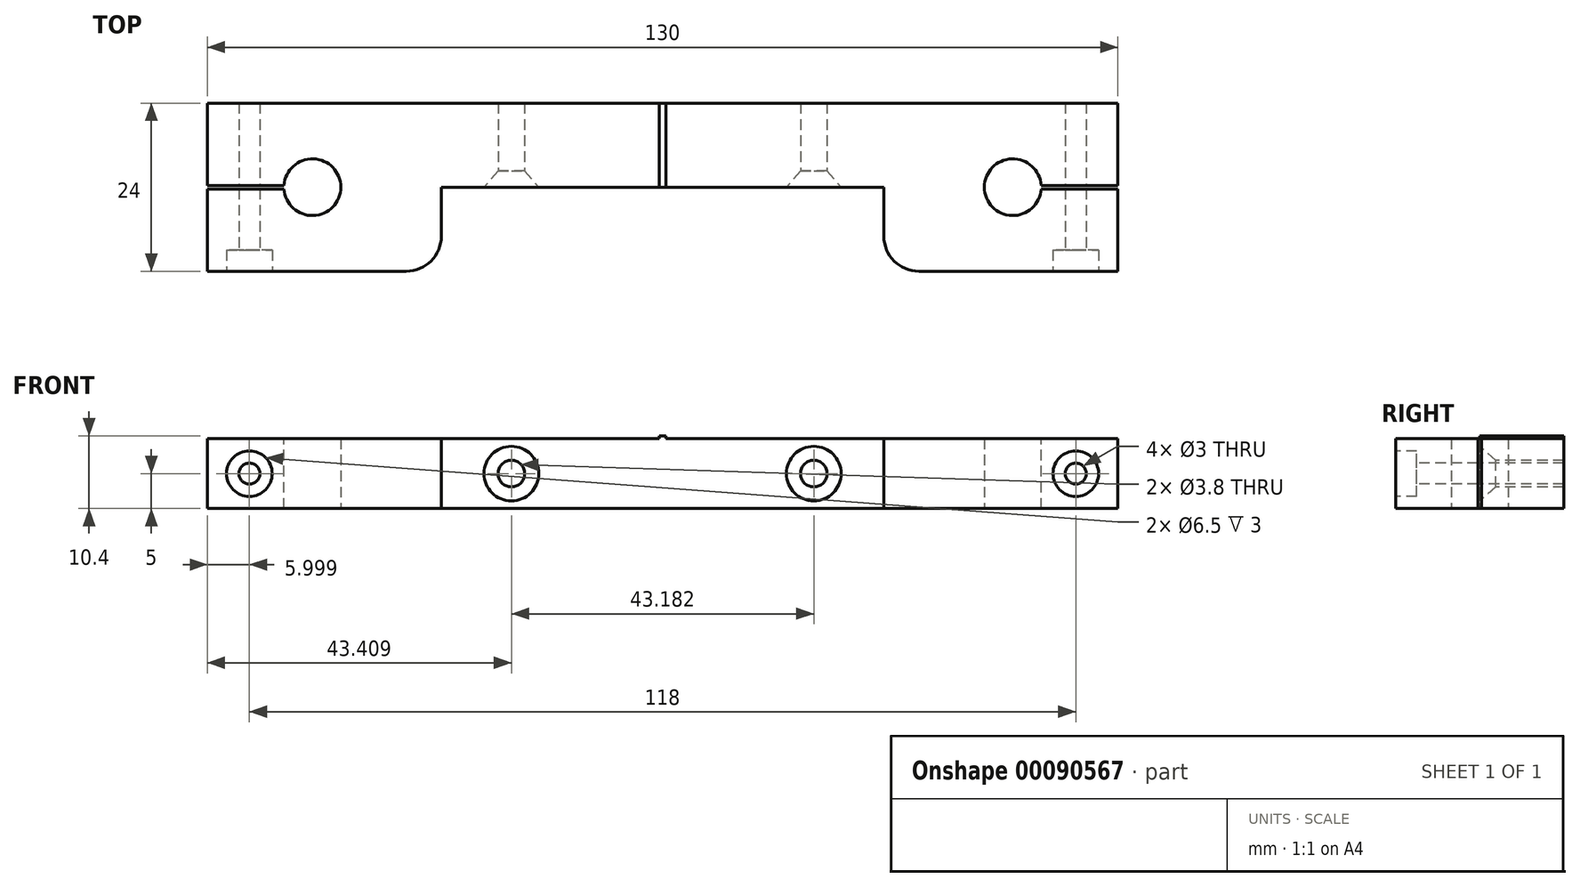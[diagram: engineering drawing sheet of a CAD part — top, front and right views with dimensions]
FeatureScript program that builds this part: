
annotation { "Feature Type Name" : "Feature", "Feature Type Description" : "" }
export const myFeature = defineFeature(function(context is Context, id is Id, definition is map)
    precondition{}
    {
        {
            var Q0;
            Q0=qCreatedBy(makeId("Top.planeOp"),FACE);
            var sketch = newSketch(context, id + "F0", { "sketchPlane" : qUnion([Q0])});
            skLineSegment(sketch, "E0.bottom", {"start": v(-62.4, -8.21) * mm, "end": v(67.6, -8.21) * mm});
            skLineSegment(sketch, "E0.top", {"start": v(-62.4, -32.21) * mm, "end": v(67.6, -32.21) * mm});
            skLineSegment(sketch, "E0.left", {"start": v(-62.4, -8.21) * mm, "end": v(-62.4, -32.21) * mm});
            skLineSegment(sketch, "E0.right", {"start": v(67.6, -8.21) * mm, "end": v(67.6, -32.21) * mm});
            skLineSegment(sketch, "E1", {"start": v(-62.4, -20.21) * mm, "end": v(67.6, -20.21) * mm, "construction": true});
            skLineSegment(sketch, "E2", {"start": v(-47.4, -8.21) * mm, "end": v(-47.4, -32.21) * mm, "construction": true});
            skCircle(sketch, "E3", {"center": v(-47.4, -20.21) * mm, "radius": 4.05 * mm});
            skCircle(sketch, "E4.1.0.0", {"center": v(52.6, -20.21) * mm, "radius": 4.05 * mm});
            skLineSegment(sketch, "E4.direction1", {"start": v(-47.4, -20.21) * mm, "end": v(52.6, -20.21) * mm, "construction": true});
            skPoint(sketch, "E5", {"position": v(2.6, -32.21) * mm});
            skLineSegment(sketch, "E6.bottom", {"start": v(-29, -32.21) * mm, "end": v(34.2, -32.21) * mm});
            skLineSegment(sketch, "E6.top", {"start": v(-29, -20.21) * mm, "end": v(34.2, -20.21) * mm});
            skLineSegment(sketch, "E6.left", {"start": v(-29, -32.21) * mm, "end": v(-29, -20.21) * mm});
            skLineSegment(sketch, "E6.right", {"start": v(34.2, -32.21) * mm, "end": v(34.2, -20.21) * mm});
            skPoint(sketch, "E7", {"position": v(2.6, -20.21) * mm});
            skSolve(sketch);
        }
        {
            var Q0;
            Q0=makeQuery(id+"F0.imprint","IMPRINT",FACE,{"disambiguationData":[TD([[makeQuery(id+"F0.imprint","IMPRINT",EDGE,{"derivedFrom":sQuery(id+"F0.wireOp",EDGE,"E0.bottom")}),-1.0]])]});
            extrude(context, id + "F1", {"entities" : qUnion([Q0]), "depth" : 10 * mm});
        }
        {
            var Q0;
            Q0=makeQuery(id+"F1.opExtrude","SWEPT_EDGE",EDGE,{"disambiguationData":[OSD([sQuery(id+"F0.wireOp",EDGE,"E0.top"),sQuery(id+"F0.wireOp",EDGE,"E6.bottom"),sQuery(id+"F0.wireOp",EDGE,"E6.right")])]});
            var Q1;
            Q1=makeQuery(id+"F1.opExtrude","SWEPT_EDGE",EDGE,{"disambiguationData":[OSD([sQuery(id+"F0.wireOp",EDGE,"E0.top"),sQuery(id+"F0.wireOp",EDGE,"E6.bottom"),sQuery(id+"F0.wireOp",EDGE,"E6.left")])]});
            fillet(context, id + "F2", {"entities" : qUnion([Q0, Q1]), "radius" : 5 * mm, "tangentPropagation" : true, "allowEdgeOverflow" : false});
        }
        {
            var Q0;
            Q0=makeQuery(id+"F1.opExtrude","SWEPT_FACE",FACE,{"disambiguationData":[OSD([sQuery(id+"F0.wireOp",EDGE,"E6.top")])]});
            var sketch = newSketch(context, id + "F3", { "sketchPlane" : qUnion([Q0])});
            skLineSegment(sketch, "E8", {"start": v(-29, 5) * mm, "end": v(34.2, 5) * mm, "construction": true});
            skLineSegment(sketch, "E9", {"start": v(-19, 10) * mm, "end": v(-19, 0) * mm, "construction": true});
            skLineSegment(sketch, "E10", {"start": v(24.2, 10) * mm, "end": v(24.2, 0) * mm, "construction": true});
            skPoint(sketch, "E11", {"position": v(-19, 5) * mm});
            skPoint(sketch, "E12", {"position": v(24.2, 5) * mm});
            skSolve(sketch);
        }
        {
            var Q0;
            Q0=sQuery(id+"F3.wireOp",VERTEX,"E11");
            var Q1;
            Q1=sQuery(id+"F3.wireOp",VERTEX,"E12");
            var Q2;
            Q2=makeQuery(id+"F1.opExtrude","SWEPT_BODY",BODY,{"disambiguationData":[OSD([sQuery(id+"F0.wireOp",EDGE,"E0.bottom"),sQuery(id+"F0.wireOp",EDGE,"E0.top"),sQuery(id+"F0.wireOp",EDGE,"E0.left"),sQuery(id+"F0.wireOp",EDGE,"E0.right"),sQuery(id+"F0.wireOp",EDGE,"E3"),sQuery(id+"F0.wireOp",EDGE,"E4.1.0.0"),sQuery(id+"F0.wireOp",EDGE,"E6.top"),sQuery(id+"F0.wireOp",EDGE,"E6.left"),sQuery(id+"F0.wireOp",EDGE,"E6.right")])]});
            hole(context, id + "F4", {"style" : HoleStyle.C_SINK, "endStyle" : HoleEndStyle.THROUGH, "standardTappedOrClearance" : lookupTablePath({ "standard" : "ANSI", "fit" : "Normal (ASME)", "size" : "#6", "type" : "Clearance" }), "standardBlindInLast" : lookupTablePath({ "fit" : "Free", "standard" : "ANSI", "size" : "#6", "type" : "Clearance" }), "holeDiameter" : 3.8 * mm, "cSinkDiameter" : 7.8 * mm, "cSinkAngle" : 82 * degree, "locations" : qUnion([Q0, Q1]), "scope" : qUnion([Q2]), "isTappedThrough" : true});
        }
        {
            var Q0;
            Q0=makeQuery(id+"F1.opExtrude","CAP_FACE",FACE,{"disambiguationData":[OSD([sQuery(id+"F0.wireOp",EDGE,"E0.bottom"),sQuery(id+"F0.wireOp",EDGE,"E0.top"),sQuery(id+"F0.wireOp",EDGE,"E0.left"),sQuery(id+"F0.wireOp",EDGE,"E0.right"),sQuery(id+"F0.wireOp",EDGE,"E3"),sQuery(id+"F0.wireOp",EDGE,"E4.1.0.0"),sQuery(id+"F0.wireOp",EDGE,"E6.top"),sQuery(id+"F0.wireOp",EDGE,"E6.left"),sQuery(id+"F0.wireOp",EDGE,"E6.right")])],"isStart":false});
            var sketch = newSketch(context, id + "F5", { "sketchPlane" : qUnion([Q0])});
            skPoint(sketch, "E13", {"position": v(2.6, -8.21) * mm});
            skPoint(sketch, "E14", {"position": v(2.6, -20.21) * mm});
            skLineSegment(sketch, "E15", {"start": v(2.1, -8.21) * mm, "end": v(2.1, -20.21) * mm});
            skLineSegment(sketch, "E16", {"start": v(3.1, -8.21) * mm, "end": v(3.1, -20.21) * mm});
            skSolve(sketch);
        }
        {
            var Q0;
            {var subQ0=sQuery(id+"F5.wireOp",EDGE,"E15");Q0=makeQuery(id+"F5.imprint","IMPRINT",FACE,{"disambiguationData":[TD([[makeQuery(id+"F5.imprint","IMPRINT",EDGE,{"derivedFrom":subQ0}),1.0]])]});}
            extrude(context, id + "F6", {"entities" : qUnion([Q0]), "operationType" : NewBodyOperationType.ADD, "depth" : 0.4 * mm});
        }
        {
            var Q0;
            {var subQ0=sQuery(id+"F0.wireOp",EDGE,"E3");var subQ1=sQuery(id+"F0.wireOp",EDGE,"E0.left");var subQ2=sQuery(id+"F0.wireOp",EDGE,"E0.top");var subQ3=sQuery(id+"F0.wireOp",EDGE,"E6.left");var subQ5=sQuery(id+"F0.wireOp",EDGE,"E0.bottom");var subQ6=sQuery(id+"F0.wireOp",EDGE,"E6.top");Q0=makeQuery(id+"F6.boolean.opBoolean","SPLIT",FACE,{"disambiguationData":[TD([makeQuery(id+"F1.opExtrude","SWEPT_FACE",FACE,{"disambiguationData":[OSD([subQ1])]})])],"derivedFrom":makeQuery(id+"F1.opExtrude","CAP_FACE",FACE,{"disambiguationData":[OSD([subQ5,subQ2,subQ1,sQuery(id+"F0.wireOp",EDGE,"E0.right"),subQ0,sQuery(id+"F0.wireOp",EDGE,"E4.1.0.0"),subQ6,subQ3,sQuery(id+"F0.wireOp",EDGE,"E6.right")])],"isStart":false})});}
            var sketch = newSketch(context, id + "F7", { "sketchPlane" : qUnion([Q0])});
            skLineSegment(sketch, "E17.bottom", {"start": v(-62.4, -19.96) * mm, "end": v(-51.44, -19.96) * mm});
            skLineSegment(sketch, "E17.top", {"start": v(-62.4, -20.46) * mm, "end": v(-51.44, -20.46) * mm});
            skLineSegment(sketch, "E17.left", {"start": v(-62.4, -19.96) * mm, "end": v(-62.4, -20.46) * mm});
            skLineSegment(sketch, "E17.right", {"start": v(-51.44, -19.96) * mm, "end": v(-51.44, -20.46) * mm});
            skCircle(sketch, "E18.0", {"center": v(-47.4, -20.21) * mm, "radius": 4.05 * mm});
            skPoint(sketch, "E19", {"position": v(-51.44, -20.21) * mm});
            skCircle(sketch, "E20.0", {"center": v(52.6, -20.21) * mm, "radius": 4.05 * mm});
            skLineSegment(sketch, "E21.bottom", {"start": v(56.64, -19.96) * mm, "end": v(67.6, -19.96) * mm});
            skLineSegment(sketch, "E21.top", {"start": v(56.64, -20.46) * mm, "end": v(67.6, -20.46) * mm});
            skLineSegment(sketch, "E21.left", {"start": v(56.64, -19.96) * mm, "end": v(56.64, -20.46) * mm});
            skLineSegment(sketch, "E21.right", {"start": v(67.6, -19.96) * mm, "end": v(67.6, -20.46) * mm});
            skPoint(sketch, "E22", {"position": v(56.64, -20.21) * mm});
            skSolve(sketch);
        }
        {
            var Q0;
            {var subQ1=sQuery(id+"F7.wireOp",EDGE,"E21.bottom");Q0=makeQuery(id+"F7.imprint","IMPRINT",FACE,{"disambiguationData":[TD([[makeQuery(id+"F7.imprint","IMPRINT",EDGE,{"derivedFrom":subQ1}),-1.0]])]});}
            var Q1;
            {var subQ0=sQuery(id+"F7.wireOp",EDGE,"E17.bottom");Q1=makeQuery(id+"F7.imprint","IMPRINT",FACE,{"disambiguationData":[TD([[makeQuery(id+"F7.imprint","IMPRINT",EDGE,{"derivedFrom":subQ0}),-1.0]])]});}
            var Q2;
            {var subQ0=sQuery(id+"F7.wireOp",EDGE,"E17.right");Q2=makeQuery(id+"F7.imprint","IMPRINT",FACE,{"disambiguationData":[TD([[makeQuery(id+"F7.imprint","IMPRINT",EDGE,{"derivedFrom":subQ0}),-1.0]])]});}
            var Q3;
            {var subQ0=sQuery(id+"F7.wireOp",EDGE,"E21.left");Q3=makeQuery(id+"F7.imprint","IMPRINT",FACE,{"disambiguationData":[TD([[makeQuery(id+"F7.imprint","IMPRINT",EDGE,{"derivedFrom":subQ0}),1.0]])]});}
            extrude(context, id + "F8", {"entities" : qUnion([Q0, Q1, Q2, Q3]), "operationType" : NewBodyOperationType.REMOVE, "oppositeDirection" : true, "depth" : 25 * mm});
        }
        {
            var Q0;
            {var subQ0=sQuery(id+"F0.wireOp",EDGE,"E0.top");Q0=makeQuery(id+"F1.opExtrude","SWEPT_FACE",FACE,{"disambiguationData":[OSD([subQ0]),TDD([makeQuery(id+"F0.imprint","IMPRINT",EDGE,{"disambiguationData":[TD([[makeQuery(id+"F0.imprint","INTERSECT",VERTEX,{"derivedFrom":[subQ0,sQuery(id+"F0.wireOp",EDGE,"E0.left")]}),-1.0]])],"derivedFrom":subQ0})])]});}
            var sketch = newSketch(context, id + "F9", { "sketchPlane" : qUnion([Q0])});
            skLineSegment(sketch, "E23", {"start": v(-62.4, 5) * mm, "end": v(-34, 5) * mm, "construction": true});
            skLineSegment(sketch, "E24", {"start": v(-56.4, 10) * mm, "end": v(-56.4, 0) * mm, "construction": true});
            skPoint(sketch, "E25", {"position": v(-56.4, 5) * mm});
            skLineSegment(sketch, "E26.0.0", {"start": v(67.6, 10) * mm, "end": v(39.2, 10) * mm});
            skLineSegment(sketch, "E26.0.1", {"start": v(39.2, 10) * mm, "end": v(39.2, 0) * mm});
            skLineSegment(sketch, "E26.0.2", {"start": v(39.2, 0) * mm, "end": v(67.6, 0) * mm});
            skLineSegment(sketch, "E26.0.3", {"start": v(67.6, 0) * mm, "end": v(67.6, 10) * mm});
            skLineSegment(sketch, "E27", {"start": v(67.6, 5) * mm, "end": v(39.2, 5) * mm, "construction": true});
            skLineSegment(sketch, "E28", {"start": v(61.6, 10) * mm, "end": v(61.6, 0) * mm, "construction": true});
            skPoint(sketch, "E29", {"position": v(61.6, 5) * mm});
            skSolve(sketch);
        }
        {
            var Q0;
            Q0=sQuery(id+"F9.wireOp",VERTEX,"E29");
            var Q1;
            Q1=sQuery(id+"F9.wireOp",VERTEX,"E25");
            var Q2;
            Q2=makeQuery(id+"F1.opExtrude","SWEPT_BODY",BODY,{"disambiguationData":[OSD([sQuery(id+"F0.wireOp",EDGE,"E0.bottom"),sQuery(id+"F0.wireOp",EDGE,"E0.top"),sQuery(id+"F0.wireOp",EDGE,"E0.left"),sQuery(id+"F0.wireOp",EDGE,"E0.right"),sQuery(id+"F0.wireOp",EDGE,"E3"),sQuery(id+"F0.wireOp",EDGE,"E4.1.0.0"),sQuery(id+"F0.wireOp",EDGE,"E6.top"),sQuery(id+"F0.wireOp",EDGE,"E6.left"),sQuery(id+"F0.wireOp",EDGE,"E6.right")])]});
            hole(context, id + "F10", {"style" : HoleStyle.C_BORE, "endStyle" : HoleEndStyle.THROUGH, "standardTappedOrClearance" : lookupTablePath({ "standard" : "ISO", "size" : "3", "type" : "Drilled" }), "standardBlindInLast" : lookupTablePath({ "standard" : "ISO", "size" : "3", "type" : "Drilled" }), "holeDiameter" : 3 * mm, "cBoreDiameter" : 6.5 * mm, "cBoreDepth" : 3 * mm, "locations" : qUnion([Q0, Q1]), "scope" : qUnion([Q2]), "isTappedThrough" : true});
        }
    });
